MODEL slx_94b4017ae5c2
KIND model
BLOCK [Reference] Band-Limited White Noise  REF=simulink/Sources/Band-Limited
White Noise
  Cov = [0.1]
  Ports = [0, 1]
  SourceBlock = simulink/Sources/Band-Limited\nWhite Noise
  SourceType = Band-Limited White Noise.
  Ts = 0.1
  VectorParams1D = on
  seed = [23341]
BLOCK [Scope] Input
  DataFormat = StructureWithTime
  Floating = off
  NumInputPorts = 1
  Ports = [1]
  SaveName = ScopeData2
  ShowLegends = off
  TimeRange = 10
  YMax = 1
  YMin = -1
BLOCK [Scope] Output
  DataFormat = StructureWithTime
  Floating = off
  NumInputPorts = 1
  Ports = [1]
  SaveName = ScopeData1
  ShowLegends = off
  TimeRange = 10
  YMax = 1
  YMin = -1
BLOCK [Integrator] Process
  Ports = [1, 1]
BLOCK [Scope] Schedule
  DataFormat = StructureWithTime
  Floating = off
  LimitDataPoints = off
  NumInputPorts = 1
  Ports = [1]
  ShowLegends = off
  YMax = 2
  YMin = 0
  ZoomMode = xonly
BLOCK [Sum] Sum
  IconShape = round
  Inputs = ++|
  Ports = [2, 1]
BLOCK [Reference] TrueTime Kernel  REF=truetime/TrueTime Kernel  (lib defined in slx_0362a698a4ec)
  Ports = [1, 2]
  SourceBlock = truetime/TrueTime Kernel
  args = []
  battery = off
  clockoffsetdrift = [0 0]
  ninputsoutputs = [1 1]
  ntriggers = 0
  nwnodenbr = []
  poweroutput = off
  schedoutput = on
  sfun = simple_init
  trigtype = falling
ANNOTATION (root): TrueTime 2.0 A Simple Example <copyright redacted>
LINE Band-Limited White Noise:1 -> Sum:1
NET Process:1 -> Output:1, TrueTime Kernel:1
LINE Sum:1 -> Process:1
NET TrueTime Kernel:1 -> Input:1, Sum:2
LINE TrueTime Kernel:2 -> Schedule:1
note: NET lines group one-source signal fan-out (src -> all destinations, sorted); 1:1 wires keep LINE
